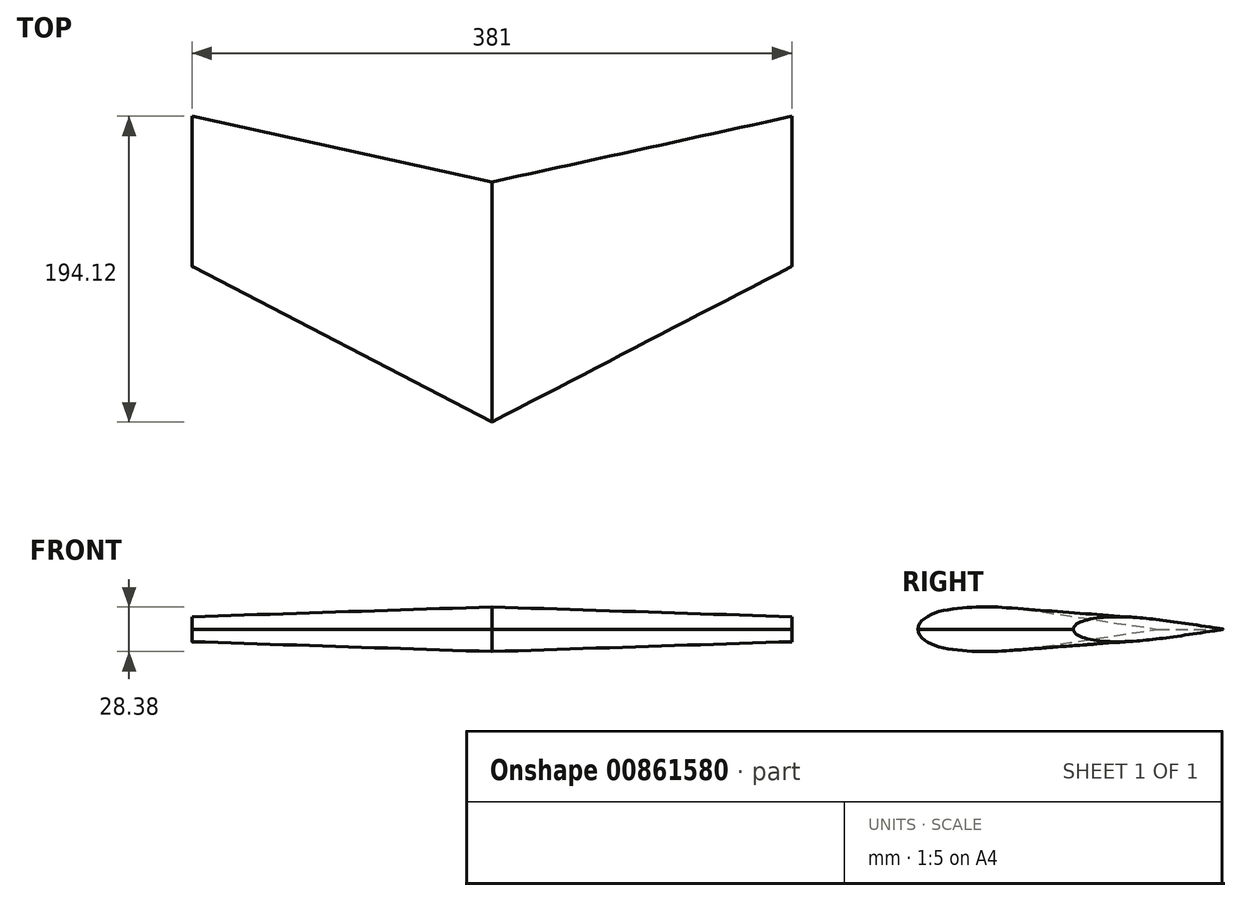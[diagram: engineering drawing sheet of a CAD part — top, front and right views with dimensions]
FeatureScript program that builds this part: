
annotation { "Feature Type Name" : "Feature", "Feature Type Description" : "" }
export const myFeature = defineFeature(function(context is Context, id is Id, definition is map)
    precondition{}
    {
        {
            var Q0;
            Q0=qCreatedBy(makeId("Right.planeOp"),FACE);
            var sketch = newSketch(context, id + "F0", { "sketchPlane" : qUnion([Q0])});
            skFitSpline(sketch, "E0", {"points": [v(-74.65, 0) * mm, v(-40.39, 13.94) * mm, v(77.75, 0) * mm], "startDerivative": vector(12.57, 91.45) * mm, "endDerivative": vector(363.32, -53.39) * mm});
            skFitSpline(sketch, "E1.MirrorCS", {"points": [v(-74.65, 0) * mm, v(-40.39, -13.94) * mm, v(77.75, 0) * mm], "startDerivative": vector(12.57, -91.45) * mm, "endDerivative": vector(363.32, 53.39) * mm});
            skSolve(sketch);
        }
        {
            var Q0;
            Q0=qCreatedBy(makeId("Right.planeOp"),FACE);
            cPlane(context, id + "F1", {"entities" : qUnion([Q0]), "cplaneType" : CPlaneType.OFFSET, "offset" : 190.5 * mm, "oppositeDirection" : true, "width" : 152.4 * mm, "height" : 152.4 * mm});
        }
        {
            var Q0;
            Q0=qCreatedBy(id+"F1.planeOp",FACE);
            var sketch = newSketch(context, id + "F2", { "sketchPlane" : qUnion([Q0])});
            skFitSpline(sketch, "E2", {"points": [v(24.13, 0) * mm, v(40.52, 7.31) * mm, v(119.47, 0) * mm], "startDerivative": vector(-0.06, 36.67) * mm, "endDerivative": vector(160.95, -25.22) * mm});
            skFitSpline(sketch, "E3.MirrorCS", {"points": [v(24.13, 0) * mm, v(40.52, -7.31) * mm, v(119.47, 0) * mm], "startDerivative": vector(-0.06, -36.67) * mm, "endDerivative": vector(160.95, 25.22) * mm});
            skSolve(sketch);
        }
        {
            var Q0;
            Q0=makeQuery(id+"F0.imprint","IMPRINT",FACE,{"disambiguationData":[TD([[makeQuery(id+"F0.imprint","IMPRINT",EDGE,{"derivedFrom":sQuery(id+"F0.wireOp",EDGE,"E0")}),-1.0]])]});
            var Q1;
            Q1=makeQuery(id+"F2.imprint","IMPRINT",FACE,{"disambiguationData":[TD([[makeQuery(id+"F2.imprint","IMPRINT",EDGE,{"derivedFrom":sQuery(id+"F2.wireOp",EDGE,"E2")}),-1.0]])]});
            loft(context, id + "F3", {"sheetProfilesArray" : [{ "sheetProfileEntities" : qUnion([Q0]) }, { "sheetProfileEntities" : qUnion([Q1]) }]});
        }
        {
            var Q0;
            Q0=makeQuery(id+"F3.opLoft","SWEPT_BODY",BODY,{"disambiguationData":[OSD([makeQuery(id+"F0.imprint","IMPRINT",FACE,{"disambiguationData":[TD([[makeQuery(id+"F0.imprint","IMPRINT",EDGE,{"derivedFrom":sQuery(id+"F0.wireOp",EDGE,"E0")}),-1.0]])]}),makeQuery(id+"F2.imprint","IMPRINT",FACE,{"disambiguationData":[TD([[makeQuery(id+"F2.imprint","IMPRINT",EDGE,{"derivedFrom":sQuery(id+"F2.wireOp",EDGE,"E2")}),-1.0]])]})])]});
            var Q1;
            Q1=qCreatedBy(makeId("Right.planeOp"),FACE);
            mirror(context, id + "F4", {"operationType" : NewBodyOperationType.ADD, "entities" : qUnion([Q0]), "mirrorPlane" : qUnion([Q1])});
        }
    });
